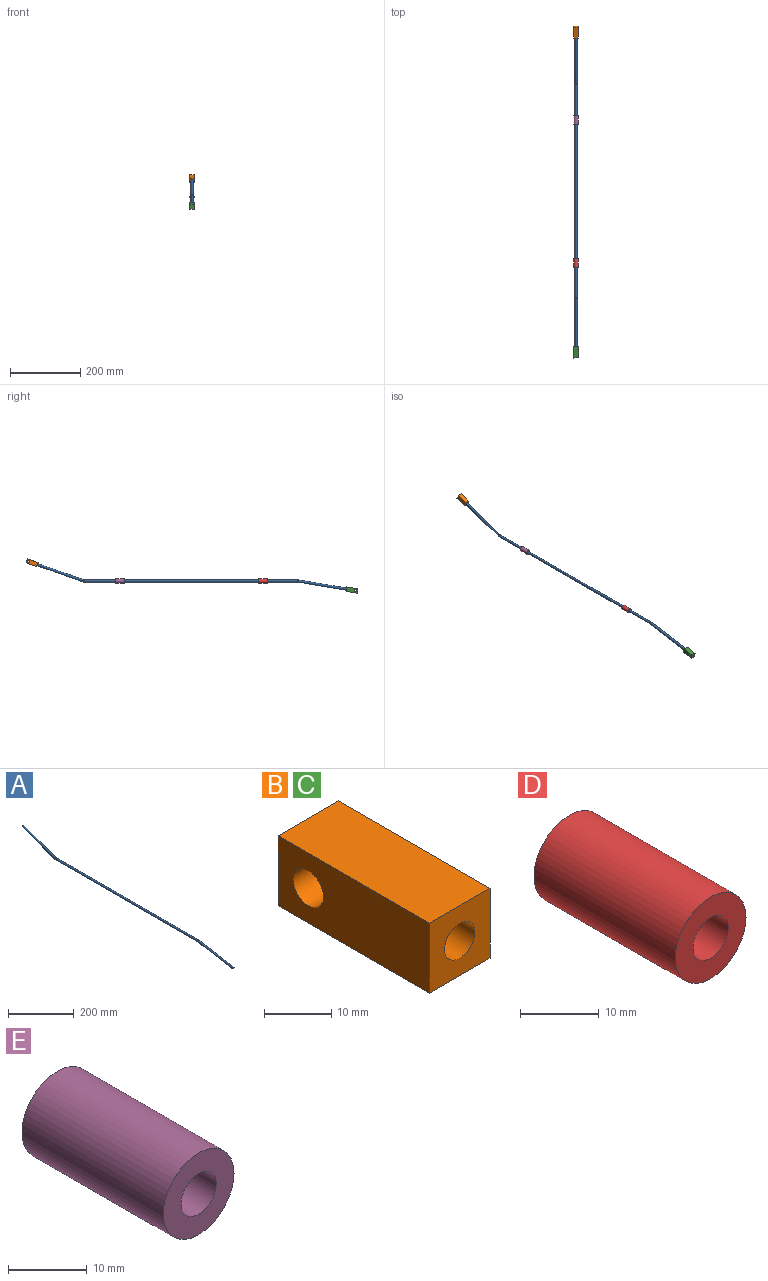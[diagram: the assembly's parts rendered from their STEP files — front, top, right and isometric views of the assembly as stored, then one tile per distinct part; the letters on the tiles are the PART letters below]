
ASSEMBLY  parts=5 mates=5
PART A: 7 faces, bbox 6.4x905.1x82.3 mm
  f0: plane 6.35x5.99mm, normal (0,0.94,0.33), area 31.7mm2, adj f2
  f1: plane 6.35x6.26mm, normal (0,-0.99,-0.17), area 31.7mm2, adj f6
  f2: cylinder r=3.17mm len=143.75mm, axis (0,-0.94,-0.33), area 2996.8mm2, adj f0,f3
  f3: torus R=12.7mm, axis (-1,0,0), area 86.1mm2, adj f2,f4
  f4: cylinder r=3.17mm len=606.36mm, axis (0,-1,0), area 12096.2mm2, adj f3,f5
  f5: torus R=12.7mm, axis (1,0,0), area 42.4mm2, adj f4,f6
  f6: cylinder r=3.17mm len=150.28mm, axis (0,-0.99,-0.17), area 3019mm2, adj f1,f5
PART B: 9 faces, bbox 12.7x31.8x12.7 mm
  f0: plane 31.75x12.7mm, normal (0,0,-1), area 403.2mm2, adj f1,f3,f4,f5
  f1: plane 31.75x12.7mm, normal (1,0,0), area 371.6mm2, adj f0,f2,f4,f5,f8
  f2: plane 31.75x12.7mm, normal (0,0,1), area 403.2mm2, adj f1,f3,f4,f5
  f3: plane 31.75x12.7mm, normal (-1,0,0), area 371.6mm2, adj f0,f2,f4,f5,f8
  f4: plane 12.7x12.7mm, normal (0,1,0), area 161.3mm2, adj f0,f1,f2,f3
  f5: plane 12.7x12.7mm, normal (0,-1,0), area 129.6mm2, adj f0,f1,f2,f3,f6
  f6: cylinder r=3.17mm len=12.7mm, axis (0,-1,0), area 253.4mm2, adj f5,f7
  f7: plane 6.35x6.35mm, normal (0,-1,0), area 31.7mm2, adj f6
  f8: cylinder r=3.17mm len=12.7mm, axis (1,0,0), area 253.4mm2, adj f1,f3
PART C: same geometry as B
PART D: 4 faces, bbox 12.7x25.4x12.7 mm
  f0: cylinder r=3.17mm len=25.4mm, axis (0,-1,0), area 506.7mm2, adj f2,f3
  f1: cylinder r=6.35mm len=25.4mm, axis (0,-1,0), area 1013.4mm2, adj f2,f3
  f2: plane 12.7x12.7mm, normal (0,1,0), area 95mm2, adj f0,f1
  f3: plane 12.7x12.7mm, normal (0,-1,0), area 95mm2, adj f0,f1
PART E: 4 faces, bbox 12.7x25.4x12.7 mm
  f0: cylinder r=3.17mm len=25.4mm, axis (0,1,0), area 506.7mm2, adj f2,f3
  f1: cylinder r=6.35mm len=25.4mm, axis (0,1,0), area 1013.4mm2, adj f2,f3
  f2: plane 12.7x12.7mm, normal (0,-1,0), area 95mm2, adj f0,f1
  f3: plane 12.7x12.7mm, normal (0,1,0), area 95mm2, adj f0,f1
PLACE A rot(axis=(0,-1,0),0.4deg) t=(0,-14.48,0)mm
PLACE B rot(axis=(1,-0.02,0),19.5deg) t=(-0.29,422.59,46.57)mm
PLACE C rot(axis=(-1,0,0),170.4deg) t=(0.15,-456.47,-23.28)mm
PLACE D t=(0,-31.8,0)mm
PLACE E at identity fixed
MATE cylindrical A.f4 <-> E.f0  axis (0,-1,0) through (0,-14.48,0)mm
MATE cylindrical A.f4 <-> D.f0  axis (0,-1,0) through (0,-14.48,0)mm
MATE fastened C.f6 <-> A.f6  axis (0,0.99,0.17) through (0.16,-468.99,-25.4)mm
MATE fastened A.f2 <-> B.f6  axis (0,0.94,0.33) through (-0.32,434.56,50.8)mm
MATE fastened E.f0 <-> D.f0  axis (0,1,0) through (0,187.3,0)mm
